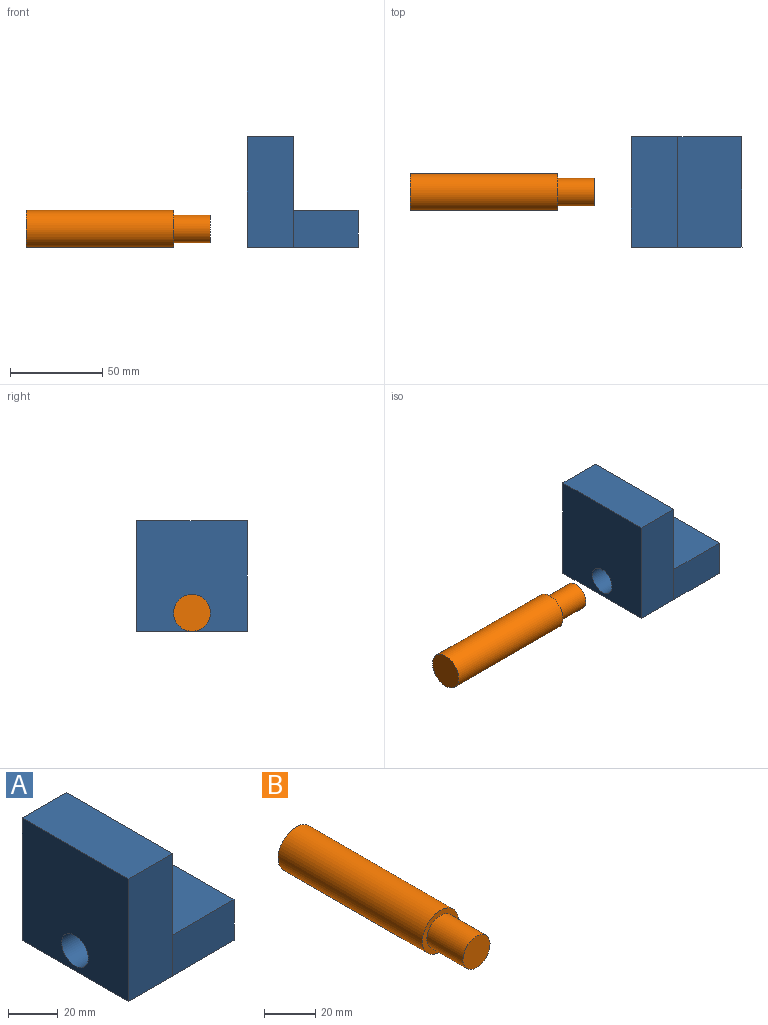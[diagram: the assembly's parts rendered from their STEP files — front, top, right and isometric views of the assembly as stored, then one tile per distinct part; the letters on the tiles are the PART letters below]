
ASSEMBLY  parts=2 mates=1
PART A: 14 faces, bbox 60x60x60 mm
  f0: plane 60x60mm, normal (1,0,0), area 2421.4mm2, adj f1,f3,f4,f5,f6,f11
  f1: plane 60x25mm, normal (0,1,0), area 1494.7mm2, adj f0,f2,f4,f5,f10,f11
  f2: plane 60x60mm, normal (-1,0,0), area 3423.3mm2, adj f1,f3,f4,f5,f13
  f3: plane 60x25mm, normal (0,-1,0), area 1500mm2, adj f0,f2,f4,f5
  f4: plane 60x25mm, normal (0,0,1), area 1500mm2, adj f0,f1,f2,f3
  f5: plane 60.01x60mm, normal (0,0,-1), area 3592.2mm2, adj f0,f1,f2,f3,f6,f7,f8,f9
  f6: plane 20x1.06mm, normal (-1,0,0), area 21.2mm2, adj f0,f5,f7,f11
  f7: plane 35x20mm, normal (0,-1,0), area 700mm2, adj f5,f6,f8,f11
  f8: plane 60x20mm, normal (1,0,0), area 1200mm2, adj f5,f7,f9,f11
  f9: plane 35x20mm, normal (0,1,0), area 700mm2, adj f5,f8,f10,f11
  f10: plane 20x0.01mm, normal (-1,0,0), area 0.2mm2, adj f1,f5,f9,f11
  f11: plane 60x35.27mm, normal (0,0,1), area 2092.2mm2, adj f0,f1,f6,f7,f8,f9,f10
  f12: cone r=0mm half-angle=59deg, axis (-1,0,0), area 206.2mm2, adj f13
  f13: cylinder r=7.5mm len=20mm, axis (-1,0,0), area 942.5mm2, adj f2,f12
PART B: 5 faces, bbox 20x100x20 mm
  f0: cylinder r=7.5mm len=20mm, axis (0,1,0), area 942.5mm2, adj f1,f4
  f1: plane 15x15mm, normal (0,-1,0), area 176.7mm2, adj f0
  f2: cylinder r=10mm len=80mm, axis (0,-1,0), area 5026.5mm2, adj f3,f4
  f3: plane 20x20mm, normal (0,1,0), area 314.2mm2, adj f2
  f4: plane 20x20mm, normal (0,-1,0), area 137.4mm2, adj f0,f2
PLACE A t=(17.28,26.19,-5.42)mm
PLACE B rot(axis=(0.71,-0.71,0),180deg) t=(-52.72,26.19,4.58)mm
MATE planar B.f0 <-> A.f13  axis (1,0,0) through (-32.72,26.19,4.58)mm
